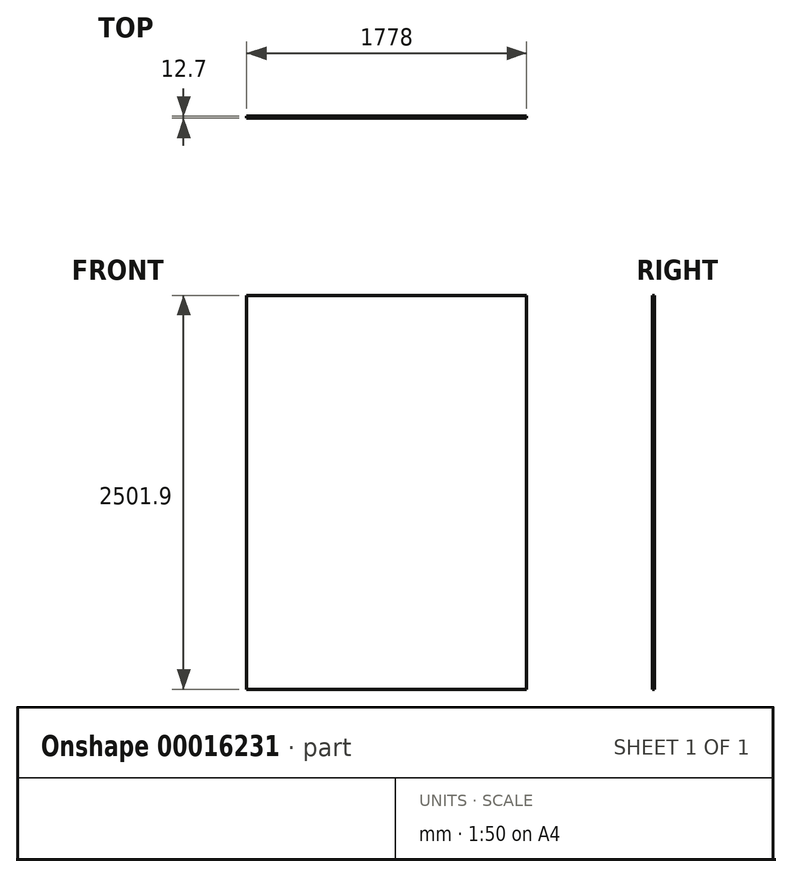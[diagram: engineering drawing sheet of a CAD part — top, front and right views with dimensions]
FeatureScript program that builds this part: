
annotation { "Feature Type Name" : "Feature", "Feature Type Description" : "" }
export const myFeature = defineFeature(function(context is Context, id is Id, definition is map)
    precondition{}
    {
        {
            var Q0;
            Q0=qCreatedBy(makeId("Front.planeOp"),FACE);
            var sketch = newSketch(context, id + "F0", { "sketchPlane" : qUnion([Q0])});
            skLineSegment(sketch, "E0", {"start": v(-889, 1250.95) * mm, "end": v(889, 1250.95) * mm});
            skLineSegment(sketch, "E1", {"start": v(-889, -1250.95) * mm, "end": v(-889, 1250.95) * mm});
            skLineSegment(sketch, "E2", {"start": v(889, 1250.95) * mm, "end": v(889, -1250.95) * mm});
            skLineSegment(sketch, "E3", {"start": v(889, -1250.95) * mm, "end": v(-889, -1250.95) * mm});
            skPoint(sketch, "E4", {"position": v(0, 1250.95) * mm});
            skPoint(sketch, "E5", {"position": v(889, 0) * mm});
            skSolve(sketch);
        }
        {
            var Q0;
            Q0=makeQuery(id+"F0.imprint","IMPRINT",FACE,{"disambiguationData":[TD([[makeQuery(id+"F0.imprint","IMPRINT",EDGE,{"derivedFrom":sQuery(id+"F0.wireOp",EDGE,"E0")}),-1.0]])]});
            extrude(context, id + "F1", {"entities" : qUnion([Q0]), "oppositeDirection" : true, "depth" : 12.7 * mm});
        }
    });
